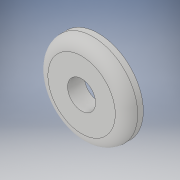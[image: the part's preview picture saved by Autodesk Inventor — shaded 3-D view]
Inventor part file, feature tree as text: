
AUTODESK INVENTOR PART (.ipt)
format: ipt  version: 2019 (Build 230136000, 136)  size: 265,728 bytes
history: native  units: mm
features: other x4, extrude x2, sketch x2, fillet x1, reference x1
ambient origin geometry x8: Origin, YZ Plane, XZ Plane, XY Plane, X Axis, Y Axis, Z Axis, Center Point
bodies: Body1 (feature_tree)
feature tree (10):
  other  "Твердое тело1"
  extrude  "Выдавливание1"  Depth=3.0mm TaperAngle=0.0deg
  fillet  "Сопряжение1"  Radius=2.0mm
  extrude  "Выдавливание2"  Depth=5.0mm
  sketch  "Эскиз1"
  reference  "Ссылка1"
  sketch  "Эскиз2"
  other  "<userpath>\Documents\GitHub\Tesla_coil_V1\3dModels\TeslaCoil.iam"
  other  "TeslaCoil.iam"
  other  "TopBox:1"
